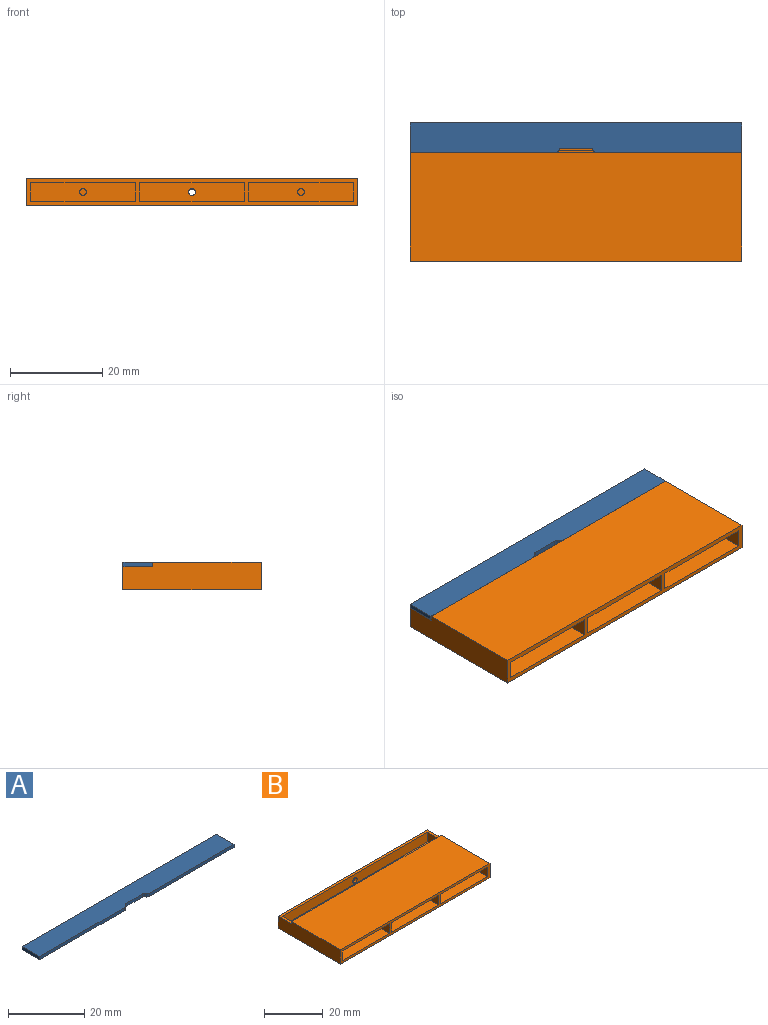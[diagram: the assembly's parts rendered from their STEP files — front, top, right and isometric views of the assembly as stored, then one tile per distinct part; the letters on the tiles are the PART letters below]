
ASSEMBLY  parts=2 mates=1
PART A: 12 faces, bbox 72x6.5x1 mm
  f0: plane 31.38x1mm, normal (0,-1,0), area 31.4mm2, adj f7,f8,f9,f10
  f1: cylinder r=0.81mm len=1mm, axis (0,0,-1), area 0.9mm2, adj f2,f8,f9,f10
  f2: plane 6x1mm, normal (0,-1,0), area 6mm2, adj f1,f3,f8,f9
  f3: cylinder r=0.81mm len=1mm, axis (0,0,-1), area 0.9mm2, adj f2,f8,f9,f11
  f4: plane 31.38x1mm, normal (0,-1,0), area 31.4mm2, adj f5,f8,f9,f11
  f5: plane 6.45x1mm, normal (1,0,0), area 6.4mm2, adj f4,f6,f8,f9
  f6: plane 72x1mm, normal (0,1,0), area 72mm2, adj f5,f7,f8,f9
  f7: plane 6.45x1mm, normal (-1,0,0), area 6.4mm2, adj f0,f6,f8,f9
  f8: plane 72x6.45mm, normal (0,0,1), area 456.9mm2, adj f0,f1,f2,f3,f4,f5,f6,f7
  f9: plane 72x6.45mm, normal (0,0,-1), area 456.9mm2, adj f0,f1,f2,f3,f4,f5,f6,f7
  f10: cylinder r=1mm len=1mm, axis (0,0,-1), area 1.1mm2, adj f0,f1,f8,f9
  f11: cylinder r=1mm len=1mm, axis (0,0,-1), area 1.1mm2, adj f3,f4,f8,f9
PART B: 32 faces, bbox 72x30x6 mm
  f0: plane 70x4mm, normal (0,1,0), area 274.7mm2, adj f1,f14,f15,f22,f28,f29,f30
  f1: plane 72x6.5mm, normal (0,0,1), area 118mm2, adj f0,f4,f5,f6,f14,f15,f16,f25
  f2: plane 22.67x4mm, normal (0,-1,0), area 88.9mm2, adj f3,f17,f20,f27,f30
  f3: plane 23x4mm, normal (-1,0,0), area 92mm2, adj f2,f13,f20,f27
  f4: plane 30x6mm, normal (1,0,0), area 173.5mm2, adj f1,f5,f13,f19,f25,f26
  f5: plane 72x5mm, normal (0,1,0), area 356.3mm2, adj f1,f4,f6,f19,f31
  f6: plane 30x6mm, normal (-1,0,0), area 173.5mm2, adj f1,f5,f13,f19,f25,f26
  f7: plane 23x4mm, normal (1,0,0), area 92mm2, adj f8,f13,f18,f23
  f8: plane 22.67x4mm, normal (0,-1,0), area 88.9mm2, adj f7,f9,f18,f23,f29
  f9: plane 23x4mm, normal (-1,0,0), area 92mm2, adj f8,f13,f18,f23
  f10: plane 23x4mm, normal (1,0,0), area 92mm2, adj f11,f13,f21,f24
  f11: plane 22.67x4mm, normal (0,-1,0), area 88.9mm2, adj f10,f12,f21,f24,f28
  f12: plane 23x4mm, normal (-1,0,0), area 92mm2, adj f11,f13,f21,f24
  f13: plane 72x6mm, normal (0,-1,0), area 160mm2, adj f3,f4,f6,f7,f9,f10,f12,f17
  f14: plane 5x4mm, normal (-1,0,0), area 20mm2, adj f0,f1,f16,f22
  f15: plane 5x4mm, normal (1,0,0), area 20mm2, adj f0,f1,f16,f22
  f16: plane 70x4mm, normal (0,-1,0), area 276.3mm2, adj f1,f14,f15,f22,f31
  f17: plane 23x4mm, normal (1,0,0), area 92mm2, adj f2,f13,f20,f27
  f18: plane 23x22.67mm, normal (0,0,1), area 521.3mm2, adj f7,f8,f9,f13
  f19: plane 72x30mm, normal (0,0,-1), area 2160mm2, adj f4,f5,f6,f13
  f20: plane 23x22.67mm, normal (0,0,1), area 521.3mm2, adj f2,f3,f13,f17
  f21: plane 23x22.67mm, normal (0,0,1), area 521.3mm2, adj f10,f11,f12,f13
  f22: plane 70x5mm, normal (0,0,1), area 350mm2, adj f0,f14,f15,f16
  f23: plane 23x22.67mm, normal (0,0,-1), area 521.3mm2, adj f7,f8,f9,f13
  f24: plane 23x22.67mm, normal (0,0,-1), area 521.3mm2, adj f10,f11,f12,f13
  f25: plane 72x1mm, normal (0,1,0), area 72mm2, adj f1,f4,f6,f26
  f26: plane 72x23.5mm, normal (0,0,1), area 1692mm2, adj f4,f6,f13,f25
  f27: plane 23x22.67mm, normal (0,0,-1), area 521.3mm2, adj f2,f3,f13,f17
  f28: cylinder r=0.75mm len=1.5mm, axis (0,-1,0), area 4.7mm2, adj f0,f11
  f29: cylinder r=0.75mm len=1.5mm, axis (0,-1,0), area 4.7mm2, adj f0,f8
  f30: cylinder r=0.75mm len=1.5mm, axis (0,-1,0), area 4.7mm2, adj f0,f2
  f31: cylinder r=1.08mm len=2.16mm, axis (0,1,0), area 6.8mm2, adj f5,f16
PLACE A t=(-2.92,3.63,7.38)mm
PLACE B t=(-2.92,-8.15,3.38)mm fixed
MATE slider A.f9 <-> B.f1  axis (0,0,-1) through (-2.92,6.85,7.38)mm
